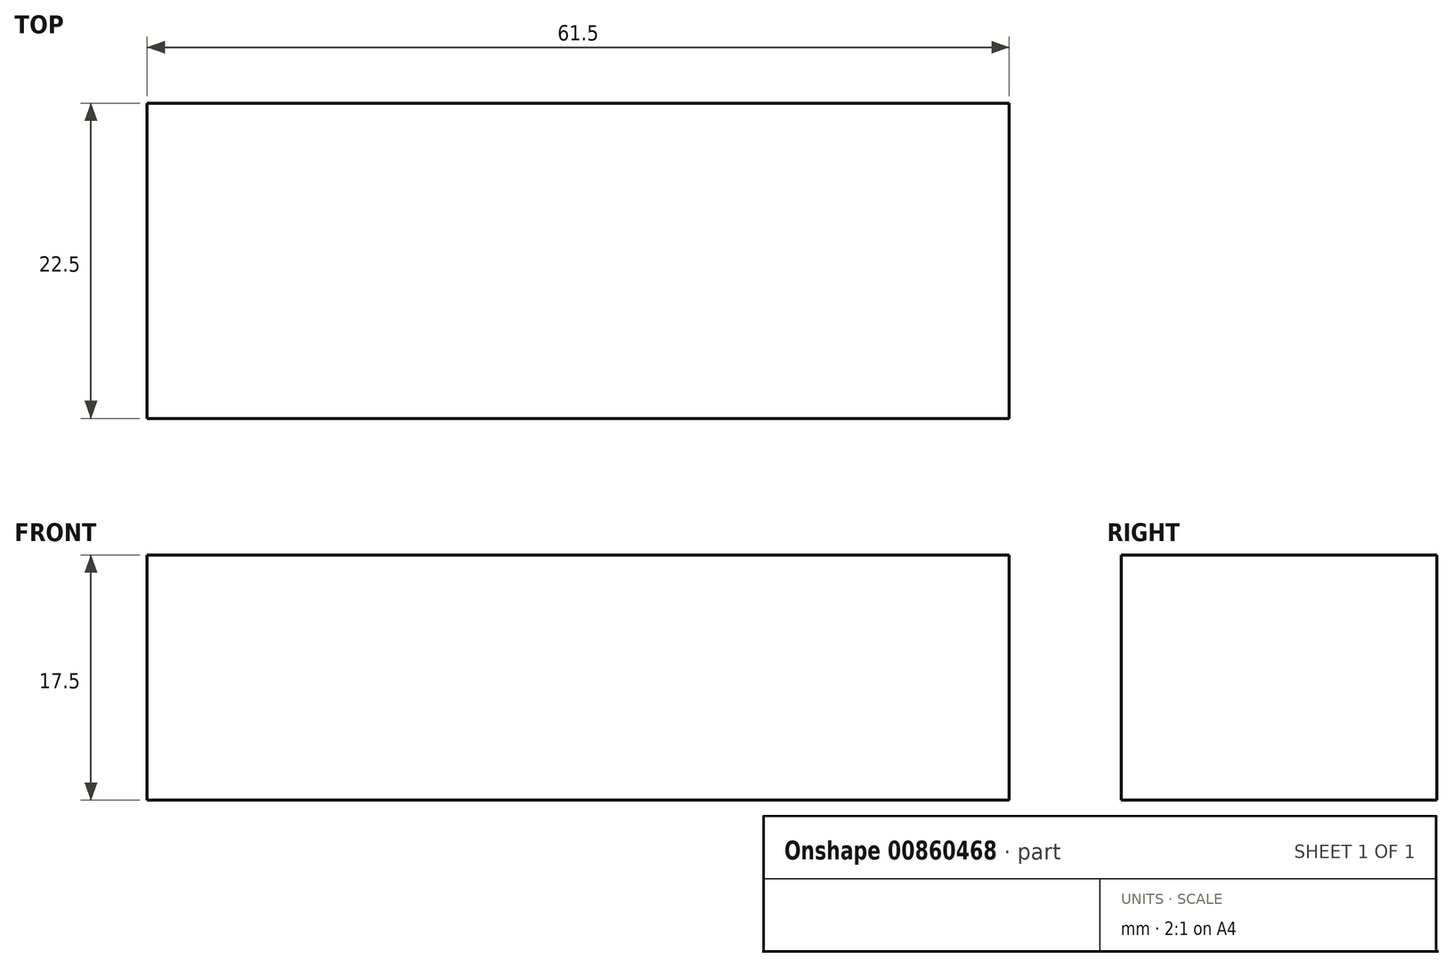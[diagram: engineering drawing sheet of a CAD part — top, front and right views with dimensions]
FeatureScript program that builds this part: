
annotation { "Feature Type Name" : "Feature", "Feature Type Description" : "" }
export const myFeature = defineFeature(function(context is Context, id is Id, definition is map)
    precondition{}
    {
        {
            var Q0;
            Q0=qCreatedBy(makeId("Front.planeOp"),FACE);
            var sketch = newSketch(context, id + "F0", { "sketchPlane" : qUnion([Q0])});
            skLineSegment(sketch, "E0.bottom", {"start": v(0, 0) * mm, "end": v(61.5, 0) * mm});
            skLineSegment(sketch, "E0.top", {"start": v(0, 17.5) * mm, "end": v(61.5, 17.5) * mm});
            skLineSegment(sketch, "E0.left", {"start": v(0, 0) * mm, "end": v(0, 17.5) * mm});
            skLineSegment(sketch, "E0.right", {"start": v(61.5, 0) * mm, "end": v(61.5, 17.5) * mm});
            skSolve(sketch);
        }
        {
            var Q0;
            Q0=makeQuery(id+"F0.imprint","IMPRINT",FACE,{"disambiguationData":[TD([[makeQuery(id+"F0.imprint","IMPRINT",EDGE,{"derivedFrom":sQuery(id+"F0.wireOp",EDGE,"E0.bottom")}),1.0]])]});
            extrude(context, id + "F1", {"entities" : qUnion([Q0]), "depth" : 22.5 * mm, "offsetDistance" : 25 * mm});
        }
    });
